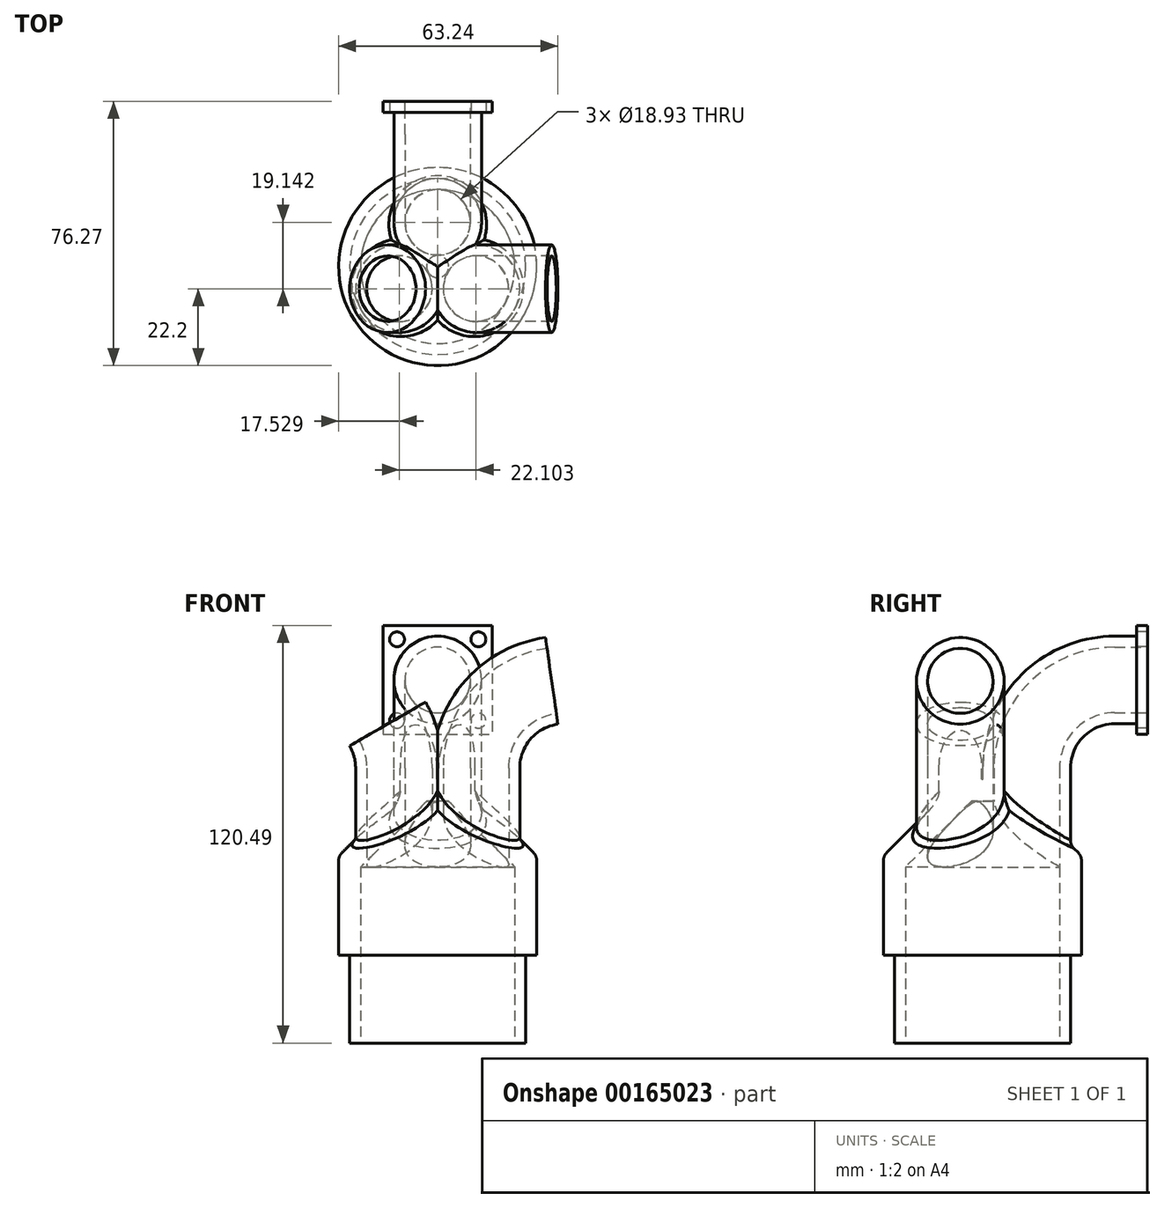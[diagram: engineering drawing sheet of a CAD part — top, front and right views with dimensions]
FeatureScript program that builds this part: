
annotation { "Feature Type Name" : "Feature", "Feature Type Description" : "" }
export const myFeature = defineFeature(function(context is Context, id is Id, definition is map)
    precondition{}
    {
        {
            var Q0;
            Q0=qCreatedBy(makeId("Top.planeOp"),FACE);
            var sketch = newSketch(context, id + "F0", { "sketchPlane" : qUnion([Q0])});
            skCircle(sketch, "E0", {"center": v(0, 0) * mm, "radius": 22.23 * mm});
            skCircle(sketch, "E1", {"center": v(0, 0) * mm, "radius": 28.58 * mm});
            skSolve(sketch);
        }
        {
            var Q0;
            Q0 = qSketchRegion(id + "F0", true);
            extrude(context, id + "F1", {"entities" : qUnion([Q0]), "depth" : 25.4 * mm});
        }
        {
            var Q0;
            Q0=makeQuery(id+"F1.opExtrude","CAP_FACE",FACE,{"disambiguationData":[OSD([sQuery(id+"F0.wireOp",EDGE,"E0"),sQuery(id+"F0.wireOp",EDGE,"E1")])],"isStart":false});
            var sketch = newSketch(context, id + "F2", { "sketchPlane" : qUnion([Q0])});
            skCircle(sketch, "E2", {"center": v(0, 0) * mm, "radius": 28.58 * mm});
            skCircle(sketch, "E3", {"center": v(0, 12.76) * mm, "radius": 9.46 * mm});
            skCircle(sketch, "E4", {"center": v(11.05, -6.38) * mm, "radius": 9.46 * mm});
            skCircle(sketch, "E5", {"center": v(-11.05, -6.38) * mm, "radius": 9.46 * mm});
            skLineSegment(sketch, "E6", {"start": v(0, 0) * mm, "end": v(0, 12.76) * mm, "construction": true});
            skLineSegment(sketch, "E7", {"start": v(0, 0) * mm, "end": v(11.05, -6.38) * mm, "construction": true});
            skLineSegment(sketch, "E8", {"start": v(0, 12.76) * mm, "end": v(11.05, -6.38) * mm, "construction": true});
            skLineSegment(sketch, "E9", {"start": v(11.05, -6.38) * mm, "end": v(-11.05, -6.38) * mm, "construction": true});
            skLineSegment(sketch, "E10", {"start": v(0, 12.76) * mm, "end": v(-11.05, -6.38) * mm, "construction": true});
            skLineSegment(sketch, "E11", {"start": v(-11.05, -6.38) * mm, "end": v(0, 0) * mm, "construction": true});
            skCircle(sketch, "E12", {"center": v(5.53, 3.2) * mm, "radius": 1.59 * mm, "construction": true});
            skSolve(sketch);
        }
        {
            var Q0;
            Q0 = qSketchRegion(id + "F2", true);
            extrude(context, id + "F3", {"entities" : qUnion([Q0]), "operationType" : NewBodyOperationType.ADD, "depth" : 25.4 * mm});
        }
        {
            var Q0;
            Q0=qCreatedBy(makeId("Front.planeOp"),FACE);
            var sketch = newSketch(context, id + "F4", { "sketchPlane" : qUnion([Q0])});
            skLineSegment(sketch, "E13.bottom", {"start": v(-3.18, 44.45) * mm, "end": v(-22.23, 44.45) * mm, "construction": true});
            skLineSegment(sketch, "E13.top", {"start": v(-3.18, 25.4) * mm, "end": v(-22.23, 25.4) * mm});
            skLineSegment(sketch, "E13.left", {"start": v(-3.18, 44.45) * mm, "end": v(-3.18, 25.4) * mm});
            skLineSegment(sketch, "E13.right", {"start": v(-22.23, 44.45) * mm, "end": v(-22.22, 25.4) * mm, "construction": true});
            skLineSegment(sketch, "E14", {"start": v(-3.18, 44.45) * mm, "end": v(-22.23, 25.4) * mm});
            skLineSegment(sketch, "E15", {"start": v(-3.18, 25.4) * mm, "end": v(0, 25.4) * mm, "construction": true});
            skSolve(sketch);
        }
        {
            var Q0;
            Q0 = qSketchRegion(id + "F4", true);
            var Q1;
            Q1=makeQuery(id+"F1.opExtrude","SWEPT_FACE",FACE,{"disambiguationData":[OSD([sQuery(id+"F0.wireOp",EDGE,"E0")])]});
            revolve(context, id + "F5", {"operationType" : NewBodyOperationType.REMOVE, "entities" : qUnion([Q0]), "axis" : qUnion([Q1]), "revolveType" : RevolveType.FULL, "oppositeDirection" : true});
        }
        {
            var Q0;
            Q0=makeQuery(id+"F3.opExtrude","CAP_FACE",FACE,{"disambiguationData":[OSD([sQuery(id+"F2.wireOp",EDGE,"E2"),sQuery(id+"F2.wireOp",EDGE,"E3"),sQuery(id+"F2.wireOp",EDGE,"E4"),sQuery(id+"F2.wireOp",EDGE,"E5")])],"isStart":true});
            extrude(context, id + "F6", {"entities" : qUnion([Q0]), "operationType" : NewBodyOperationType.REMOVE, "oppositeDirection" : true, "depth" : 19.05 * mm});
        }
        {
            var Q0;
            Q0=qCreatedBy(makeId("Right.planeOp"),FACE);
            var sketch = newSketch(context, id + "F7", { "sketchPlane" : qUnion([Q0])});
            skLineSegment(sketch, "E16", {"start": v(12.76, 50.8) * mm, "end": v(12.76, 53.98) * mm});
            skArc(sketch, "E17", {"start": v(38.16, 79.38) * mm, "mid": v(20.2, 71.94) * mm, "end": v(12.76, 53.98) * mm});
            skLineSegment(sketch, "E18", {"start": v(12.76, 53.98) * mm, "end": v(38.16, 53.98) * mm, "construction": true});
            skLineSegment(sketch, "E19", {"start": v(38.16, 53.98) * mm, "end": v(38.16, 79.38) * mm, "construction": true});
            skLineSegment(sketch, "E20", {"start": v(38.16, 79.38) * mm, "end": v(44.51, 79.38) * mm});
            skSolve(sketch);
        }
        {
            var Q0;
            Q0=makeQuery(id+"F3.opExtrude","CAP_FACE",FACE,{"disambiguationData":[OSD([sQuery(id+"F2.wireOp",EDGE,"E2"),sQuery(id+"F2.wireOp",EDGE,"E3"),sQuery(id+"F2.wireOp",EDGE,"E4"),sQuery(id+"F2.wireOp",EDGE,"E5")])],"isStart":false});
            var sketch = newSketch(context, id + "F8", { "sketchPlane" : qUnion([Q0])});
            skCircle(sketch, "E21", {"center": v(0, 12.76) * mm, "radius": 12.64 * mm});
            skCircle(sketch, "E22", {"center": v(0, 12.76) * mm, "radius": 9.46 * mm});
            skSolve(sketch);
        }
        {
            var Q0;
            Q0 = qSketchRegion(id + "F8", true);
            var Q1;
            Q1=sQuery(id+"F7.wireOp",EDGE,"E17");
            var Q2;
            Q2=sQuery(id+"F7.wireOp",EDGE,"E20");
            var Q3;
            Q3=sQuery(id+"F7.wireOp",EDGE,"E16");
            sweep(context, id + "F9", {"operationType" : NewBodyOperationType.ADD, "profiles" : qUnion([Q0]), "path" : qUnion([Q1, Q2, Q3])});
        }
        {
            var Q0;
            Q0=qCreatedBy(makeId("Front.planeOp"),FACE);
            cPlane(context, id + "F10", {"entities" : qUnion([Q0]), "cplaneType" : CPlaneType.OFFSET, "offset" : 6.38 * mm, "width" : 152.4 * mm, "height" : 152.4 * mm});
        }
        {
            var Q0;
            Q0=qCreatedBy(id+"F10.planeOp",FACE);
            var sketch = newSketch(context, id + "F11", { "sketchPlane" : qUnion([Q0])});
            skLineSegment(sketch, "E23", {"start": v(11.05, 50.8) * mm, "end": v(11.05, 53.98) * mm});
            skLineSegment(sketch, "E24", {"start": v(-11.05, 50.8) * mm, "end": v(-11.05, 53.98) * mm});
            skArc(sketch, "E25", {"start": v(32.9, 79.12) * mm, "mid": v(17.27, 70.63) * mm, "end": v(11.05, 53.98) * mm});
            skArc(sketch, "E26", {"start": v(-11.05, 53.98) * mm, "mid": v(-11.92, 60.55) * mm, "end": v(-14.45, 66.68) * mm});
            skLineSegment(sketch, "E27", {"start": v(-11.05, 53.98) * mm, "end": v(-36.45, 53.98) * mm, "construction": true});
            skLineSegment(sketch, "E28", {"start": v(11.05, 53.98) * mm, "end": v(36.45, 53.98) * mm, "construction": true});
            skLineSegment(sketch, "E29", {"start": v(32.9, 79.12) * mm, "end": v(61.58, 83.19) * mm, "construction": true});
            skLineSegment(sketch, "E30", {"start": v(-14.45, 66.67) * mm, "end": v(-39.85, 110.67) * mm, "construction": true});
            skLineSegment(sketch, "E31", {"start": v(-14.45, 66.68) * mm, "end": v(-39.85, 66.68) * mm, "construction": true});
            skLineSegment(sketch, "E32", {"start": v(-39.85, 66.68) * mm, "end": v(-39.85, 110.67) * mm, "construction": true});
            skSolve(sketch);
        }
        {
            var Q0;
            Q0=makeQuery(id+"F3.opExtrude","CAP_FACE",FACE,{"disambiguationData":[OSD([sQuery(id+"F2.wireOp",EDGE,"E2"),sQuery(id+"F2.wireOp",EDGE,"E3"),sQuery(id+"F2.wireOp",EDGE,"E4"),sQuery(id+"F2.wireOp",EDGE,"E5")])],"isStart":false});
            var sketch = newSketch(context, id + "F12", { "sketchPlane" : qUnion([Q0])});
            skCircle(sketch, "E33", {"center": v(11.05, -6.38) * mm, "radius": 9.46 * mm});
            skCircle(sketch, "E34", {"center": v(11.05, -6.38) * mm, "radius": 12.64 * mm});
            skSolve(sketch);
        }
        {
            var Q0;
            {var subQ0=sQuery(id+"F2.wireOp",EDGE,"E5");var subQ1=sQuery(id+"F2.wireOp",EDGE,"E2");var subQ2=makeQuery(id+"F3.opExtrude","CAP_FACE",FACE,{"disambiguationData":[OSD([subQ1,sQuery(id+"F2.wireOp",EDGE,"E3"),sQuery(id+"F2.wireOp",EDGE,"E4"),subQ0])],"isStart":false});Q0=makeQuery(id+"F14.boolean.opBoolean","SPLIT",FACE,{"disambiguationData":[TD([makeQuery(id+"F1.opExtrude","SWEPT_FACE",FACE,{"disambiguationData":[OSD([sQuery(id+"F0.wireOp",EDGE,"E1")])]}),makeQuery(id+"F3.opExtrude","SWEPT_FACE",FACE,{"disambiguationData":[OSD([subQ1])]}),subQ2,makeQuery(id+"F3.opExtrude","SWEPT_FACE",FACE,{"disambiguationData":[OSD([subQ0])]}),makeQuery(id+"F9.opSweep","SWEPT_FACE",FACE,{"disambiguationData":[OSD([sQuery(id+"F7.wireOp",EDGE,"E16"),sQuery(id+"F8.wireOp",EDGE,"E21")])]}),makeQuery(id+"F14.opSweep","SWEPT_FACE",FACE,{"disambiguationData":[OSD([sQuery(id+"F11.wireOp",EDGE,"E23"),sQuery(id+"F12.wireOp",EDGE,"E34")])]})])],"derivedFrom":subQ2});}
            var sketch = newSketch(context, id + "F13", { "sketchPlane" : qUnion([Q0])});
            skCircle(sketch, "E35", {"center": v(-11.05, -6.38) * mm, "radius": 9.46 * mm});
            skCircle(sketch, "E36", {"center": v(-11.05, -6.38) * mm, "radius": 12.64 * mm});
            skSolve(sketch);
        }
        {
            var Q0;
            Q0 = qSketchRegion(id + "F12", true);
            var Q1;
            Q1=sQuery(id+"F11.wireOp",EDGE,"E23");
            var Q2;
            Q2=sQuery(id+"F11.wireOp",EDGE,"E25");
            sweep(context, id + "F14", {"operationType" : NewBodyOperationType.ADD, "profiles" : qUnion([Q0]), "path" : qUnion([Q1, Q2])});
        }
        {
            var Q0;
            Q0 = qSketchRegion(id + "F13", true);
            var Q1;
            Q1=sQuery(id+"F11.wireOp",EDGE,"E24");
            var Q2;
            Q2=sQuery(id+"F11.wireOp",EDGE,"E26");
            sweep(context, id + "F15", {"operationType" : NewBodyOperationType.ADD, "profiles" : qUnion([Q0]), "path" : qUnion([Q1, Q2])});
        }
        {
            var Q0;
            Q0 = qSketchRegion(id + "F12", true);
            var Q1;
            Q1=makeQuery(id+"F5.boolean.opBoolean","COPY",FACE,{"derivedFrom":makeQuery(id+"F5.opRevolve","SWEPT_FACE",FACE,{"disambiguationData":[OSD([sQuery(id+"F4.wireOp",EDGE,"E14")])]})});
            extrude(context, id + "F16", {"entities" : qUnion([Q0]), "operationType" : NewBodyOperationType.ADD, "endBound" : BoundingType.UP_TO_SURFACE, "oppositeDirection" : true, "endBoundEntityFace" : qUnion([Q1]), "depth" : 25.4 * mm});
        }
        {
            var Q0;
            Q0=makeQuery(id+"F1.opExtrude","CAP_FACE",FACE,{"disambiguationData":[OSD([sQuery(id+"F0.wireOp",EDGE,"E0"),sQuery(id+"F0.wireOp",EDGE,"E1")])],"isStart":true});
            var sketch = newSketch(context, id + "F17", { "sketchPlane" : qUnion([Q0])});
            skCircle(sketch, "E37", {"center": v(0, 0) * mm, "radius": 22.23 * mm});
            skCircle(sketch, "E38", {"center": v(0, 0) * mm, "radius": 25.4 * mm});
            skSolve(sketch);
        }
        {
            var Q0;
            Q0 = qSketchRegion(id + "F17", true);
            extrude(context, id + "F18", {"entities" : qUnion([Q0]), "operationType" : NewBodyOperationType.ADD, "depth" : 25.4 * mm});
        }
        {
            var Q0;
            Q0=makeQuery(id+"F3.opExtrude","CAP_EDGE",EDGE,{"disambiguationData":[OSD([sQuery(id+"F2.wireOp",EDGE,"E2")])],"isStart":false});
            chamfer(context, id + "F19", {"entities" : qUnion([Q0]), "width" : 22.22 * mm, "tangentPropagation" : true});
        }
        {
            var Q0;
            Q0=makeQuery(id+"F9.opSweep","CAP_FACE",FACE,{"disambiguationData":[OSD([sQuery(id+"F7.wireOp",VERTEX,"E20.end"),sQuery(id+"F8.wireOp",EDGE,"E21"),sQuery(id+"F8.wireOp",EDGE,"E22")])],"isStart":false});
            var sketch = newSketch(context, id + "F20", { "sketchPlane" : qUnion([Q0])});
            skLineSegment(sketch, "E39.bottom", {"start": v(15.71, 95.09) * mm, "end": v(-15.71, 95.09) * mm});
            skLineSegment(sketch, "E39.top", {"start": v(15.71, 63.66) * mm, "end": v(-15.71, 63.66) * mm});
            skLineSegment(sketch, "E39.left", {"start": v(15.71, 95.09) * mm, "end": v(15.71, 63.66) * mm});
            skLineSegment(sketch, "E39.right", {"start": v(-15.71, 95.09) * mm, "end": v(-15.71, 63.66) * mm});
            skPoint(sketch, "E39.middle", {"position": v(0, 79.38) * mm});
            skLineSegment(sketch, "E40.bottom", {"start": v(11.74, 91.12) * mm, "end": v(-11.74, 91.12) * mm, "construction": true});
            skLineSegment(sketch, "E40.top", {"start": v(11.74, 67.63) * mm, "end": v(-11.74, 67.63) * mm, "construction": true});
            skLineSegment(sketch, "E40.left", {"start": v(11.74, 91.12) * mm, "end": v(11.74, 67.63) * mm, "construction": true});
            skLineSegment(sketch, "E40.right", {"start": v(-11.74, 91.12) * mm, "end": v(-11.74, 67.63) * mm, "construction": true});
            skCircle(sketch, "E41", {"center": v(11.74, 91.12) * mm, "radius": 3.97 * mm, "construction": true});
            skCircle(sketch, "E42", {"center": v(0, 79.38) * mm, "radius": 9.46 * mm});
            skCircle(sketch, "E43", {"center": v(-11.74, 91.12) * mm, "radius": 2.15 * mm});
            skCircle(sketch, "E44", {"center": v(11.74, 91.12) * mm, "radius": 2.15 * mm});
            skCircle(sketch, "E45", {"center": v(11.74, 67.63) * mm, "radius": 2.15 * mm});
            skCircle(sketch, "E46", {"center": v(-11.74, 67.63) * mm, "radius": 2.15 * mm});
            skSolve(sketch);
        }
        {
            var Q0;
            Q0 = qSketchRegion(id + "F20", true);
            extrude(context, id + "F21", {"entities" : qUnion([Q0]), "operationType" : NewBodyOperationType.ADD, "depth" : 3.17 * mm});
        }
        {
            var Q0;
            Q0=makeQuery(id+"F19.opChamfer","BLEND_FACE",FACE,{"disambiguationData":[OSD([sQuery(id+"F2.wireOp",EDGE,"E2")])]});
            fillet(context, id + "F22", {"entities" : qUnion([Q0]), "radius" : 3.17 * mm, "tangentPropagation" : true, "allowEdgeOverflow" : false});
        }
    });
